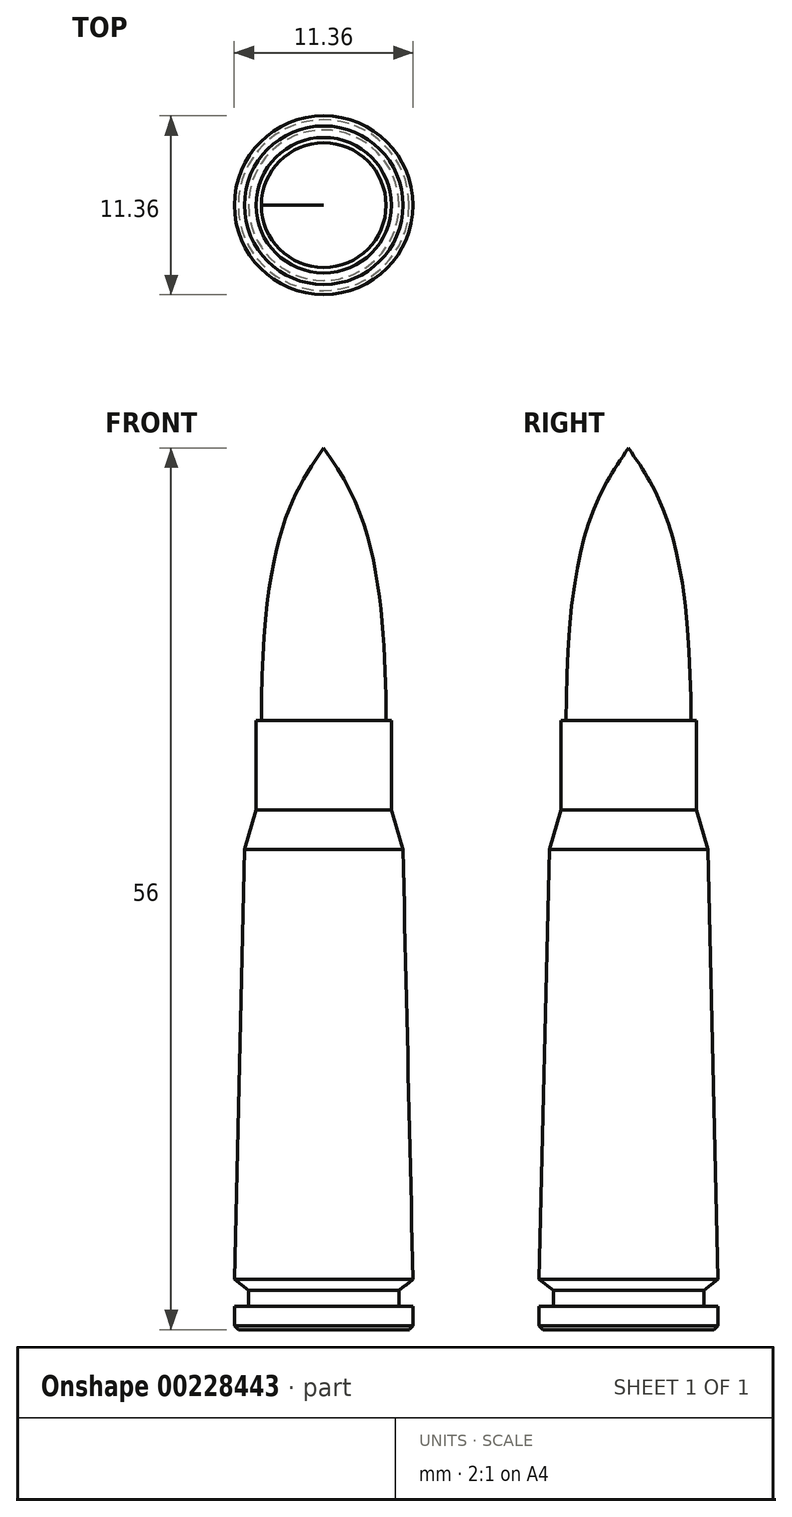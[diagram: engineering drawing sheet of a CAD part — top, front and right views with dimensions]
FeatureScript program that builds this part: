
annotation { "Feature Type Name" : "Feature", "Feature Type Description" : "" }
export const myFeature = defineFeature(function(context is Context, id is Id, definition is map)
    precondition{}
    {
        {
            var Q0;
            Q0=qCreatedBy(makeId("Top.planeOp"),FACE);
            cPlane(context, id + "F0", {"entities" : qUnion([Q0]), "cplaneType" : CPlaneType.OFFSET, "offset" : 38.7 * mm, "oppositeDirection" : true, "width" : 152.4 * mm, "height" : 152.4 * mm});
        }
        {
            var Q0;
            Q0=qCreatedBy(id+"F0.planeOp",FACE);
            cPlane(context, id + "F1", {"entities" : qUnion([Q0]), "cplaneType" : CPlaneType.OFFSET, "offset" : 56 * mm, "width" : 150 * mm, "height" : 150 * mm});
        }
        {
            var Q0;
            Q0=qCreatedBy(id+"F1.planeOp",FACE);
            var sketch = newSketch(context, id + "F2", { "sketchPlane" : qUnion([Q0])});
            skPoint(sketch, "E0", {"position": v(0, 0) * mm});
            skSolve(sketch);
        }
        {
            var Q0;
            Q0=qCreatedBy(makeId("Top.planeOp"),FACE);
            var sketch = newSketch(context, id + "F3", { "sketchPlane" : qUnion([Q0])});
            skCircle(sketch, "E1", {"center": v(0, 0) * mm, "radius": 3.96 * mm});
            skSolve(sketch);
        }
        {
            var Q0;
            Q0=makeQuery(id+"F3.imprint","IMPRINT",FACE,{"disambiguationData":[TD([[makeQuery(id+"F3.imprint","IMPRINT",EDGE,{"derivedFrom":sQuery(id+"F3.wireOp",EDGE,"E1")}),1.0]])]});
            var Q1;
            Q1=sQuery(id+"F2.wireOp",VERTEX,"E0");
            loft(context, id + "F4", {"startCondition" : LoftEndDerivativeType.NORMAL_TO_PROFILE, "startMagnitude" : 2, "sheetProfilesArray" : [{ "sheetProfileEntities" : qUnion([Q0]) }, { "sheetProfileEntities" : qUnion([Q1]) }]});
        }
        {
            var Q0;
            Q0=qCreatedBy(makeId("Top.planeOp"),FACE);
            var sketch = newSketch(context, id + "F5", { "sketchPlane" : qUnion([Q0])});
            skCircle(sketch, "E2", {"center": v(0, 0) * mm, "radius": 4.3 * mm});
            skSolve(sketch);
        }
        {
            var Q0;
            Q0=qCreatedBy(id+"F0.planeOp",FACE);
            cPlane(context, id + "F6", {"entities" : qUnion([Q0]), "cplaneType" : CPlaneType.OFFSET, "offset" : 33 * mm, "width" : 150 * mm, "height" : 150 * mm});
        }
        {
            var Q0;
            Q0=qCreatedBy(id+"F6.planeOp",FACE);
            var sketch = newSketch(context, id + "F7", { "sketchPlane" : qUnion([Q0])});
            skCircle(sketch, "E3", {"center": v(0, 0) * mm, "radius": 4.3 * mm});
            skSolve(sketch);
        }
        {
            var Q1;
            Q1=makeQuery(id+"F7.imprint","IMPRINT",FACE,{"disambiguationData":[TD([[makeQuery(id+"F7.imprint","IMPRINT",EDGE,{"derivedFrom":sQuery(id+"F7.wireOp",EDGE,"E3")}),1.0]])]});
            var Q2;
            Q2=makeQuery(id+"F5.imprint","IMPRINT",FACE,{"disambiguationData":[TD([[makeQuery(id+"F5.imprint","IMPRINT",EDGE,{"derivedFrom":sQuery(id+"F5.wireOp",EDGE,"E2")}),1.0]])]});
            loft(context, id + "F8", {"operationType" : NewBodyOperationType.ADD, "sheetProfilesArray" : [{ "sheetProfileEntities" : qUnion([Q1]) }, { "sheetProfileEntities" : qUnion([Q2]) }]});
        }
        {
            var Q0;
            Q0=qCreatedBy(id+"F0.planeOp",FACE);
            cPlane(context, id + "F9", {"entities" : qUnion([Q0]), "cplaneType" : CPlaneType.OFFSET, "offset" : 30.5 * mm, "width" : 150 * mm, "height" : 150 * mm});
        }
        {
            var Q0;
            Q0=qCreatedBy(id+"F9.planeOp",FACE);
            var sketch = newSketch(context, id + "F10", { "sketchPlane" : qUnion([Q0])});
            skCircle(sketch, "E4", {"center": v(0, 0) * mm, "radius": 5.04 * mm});
            skSolve(sketch);
        }
        {
            var Q1;
            Q1=makeQuery(id+"F10.imprint","IMPRINT",FACE,{"disambiguationData":[TD([[makeQuery(id+"F10.imprint","IMPRINT",EDGE,{"derivedFrom":sQuery(id+"F10.wireOp",EDGE,"E4")}),1.0]])]});
            var Q2;
            Q2=makeQuery(id+"F8.opLoft","CAP_FACE",FACE,{"disambiguationData":[OSD([makeQuery(id+"F7.imprint","IMPRINT",FACE,{"disambiguationData":[TD([[makeQuery(id+"F7.imprint","IMPRINT",EDGE,{"derivedFrom":sQuery(id+"F7.wireOp",EDGE,"E3")}),1.0]])]})])],"isStart":true});
            loft(context, id + "F11", {"operationType" : NewBodyOperationType.ADD, "sheetProfilesArray" : [{ "sheetProfileEntities" : qUnion([Q1]) }, { "sheetProfileEntities" : qUnion([Q2]) }]});
        }
        {
            var Q0;
            Q0=qCreatedBy(id+"F0.planeOp",FACE);
            cPlane(context, id + "F12", {"entities" : qUnion([Q0]), "cplaneType" : CPlaneType.OFFSET, "offset" : 3.2 * mm, "width" : 150 * mm, "height" : 150 * mm});
        }
        {
            var Q0;
            Q0=qCreatedBy(id+"F12.planeOp",FACE);
            var sketch = newSketch(context, id + "F13", { "sketchPlane" : qUnion([Q0])});
            skCircle(sketch, "E5", {"center": v(0, 0) * mm, "radius": 5.68 * mm});
            skSolve(sketch);
        }
        {
            var Q1;
            Q1=makeQuery(id+"F13.imprint","IMPRINT",FACE,{"disambiguationData":[TD([[makeQuery(id+"F13.imprint","IMPRINT",EDGE,{"derivedFrom":sQuery(id+"F13.wireOp",EDGE,"E5")}),1.0]])]});
            var Q2;
            Q2=makeQuery(id+"F11.opLoft","CAP_FACE",FACE,{"disambiguationData":[OSD([makeQuery(id+"F10.imprint","IMPRINT",FACE,{"disambiguationData":[TD([[makeQuery(id+"F10.imprint","IMPRINT",EDGE,{"derivedFrom":sQuery(id+"F10.wireOp",EDGE,"E4")}),1.0]])]})])],"isStart":true});
            loft(context, id + "F14", {"operationType" : NewBodyOperationType.ADD, "sheetProfilesArray" : [{ "sheetProfileEntities" : qUnion([Q1]) }, { "sheetProfileEntities" : qUnion([Q2]) }]});
        }
        {
            var Q0;
            Q0=qCreatedBy(id+"F0.planeOp",FACE);
            cPlane(context, id + "F15", {"entities" : qUnion([Q0]), "cplaneType" : CPlaneType.OFFSET, "offset" : 2.5 * mm, "width" : 150 * mm, "height" : 150 * mm});
        }
        {
            var Q0;
            Q0=qCreatedBy(id+"F15.planeOp",FACE);
            var sketch = newSketch(context, id + "F16", { "sketchPlane" : qUnion([Q0])});
            skCircle(sketch, "E6", {"center": v(0, 0) * mm, "radius": 4.78 * mm});
            skSolve(sketch);
        }
        {
            var Q1;
            Q1 = qSketchRegion(id + "F16", true);
            var Q2;
            Q2=makeQuery(id+"F14.opLoft","CAP_FACE",FACE,{"disambiguationData":[OSD([makeQuery(id+"F13.imprint","IMPRINT",FACE,{"disambiguationData":[TD([[makeQuery(id+"F13.imprint","IMPRINT",EDGE,{"derivedFrom":sQuery(id+"F13.wireOp",EDGE,"E5")}),1.0]])]})])],"isStart":true});
            loft(context, id + "F17", {"operationType" : NewBodyOperationType.ADD, "sheetProfilesArray" : [{ "sheetProfileEntities" : qUnion([Q1]) }, { "sheetProfileEntities" : qUnion([Q2]) }]});
        }
        {
            var Q0;
            Q0=makeQuery(id+"F17.opLoft","CAP_FACE",FACE,{"disambiguationData":[OSD([makeQuery(id+"F16.imprint","IMPRINT",FACE,{"disambiguationData":[TD([[makeQuery(id+"F16.imprint","IMPRINT",EDGE,{"derivedFrom":sQuery(id+"F16.wireOp",EDGE,"E6")}),1.0]])]})])],"isStart":true});
            extrude(context, id + "F18", {"entities" : qUnion([Q0]), "operationType" : NewBodyOperationType.ADD, "depth" : 1 * mm});
        }
        {
            var Q0;
            Q0=qCreatedBy(id+"F0.planeOp",FACE);
            cPlane(context, id + "F19", {"entities" : qUnion([Q0]), "cplaneType" : CPlaneType.OFFSET, "offset" : 1.5 * mm, "width" : 150 * mm, "height" : 150 * mm});
        }
        {
            var Q0;
            Q0=qCreatedBy(id+"F19.planeOp",FACE);
            var sketch = newSketch(context, id + "F20", { "sketchPlane" : qUnion([Q0])});
            skCircle(sketch, "E7", {"center": v(0, 0) * mm, "radius": 5.68 * mm});
            skSolve(sketch);
        }
        {
            var Q0;
            Q0=makeQuery(id+"F20.imprint","IMPRINT",FACE,{"disambiguationData":[TD([[makeQuery(id+"F20.imprint","IMPRINT",EDGE,{"derivedFrom":sQuery(id+"F20.wireOp",EDGE,"E7")}),1.0]])]});
            extrude(context, id + "F21", {"entities" : qUnion([Q0]), "operationType" : NewBodyOperationType.ADD, "oppositeDirection" : true, "depth" : 1.25 * mm});
        }
        {
            var Q0;
            Q0=qCreatedBy(id+"F0.planeOp",FACE);
            var sketch = newSketch(context, id + "F22", { "sketchPlane" : qUnion([Q0])});
            skCircle(sketch, "E8", {"center": v(0, 0) * mm, "radius": 5.42 * mm});
            skSolve(sketch);
        }
        {
            var Q1;
            Q1=makeQuery(id+"F22.imprint","IMPRINT",FACE,{"disambiguationData":[TD([[makeQuery(id+"F22.imprint","IMPRINT",EDGE,{"derivedFrom":sQuery(id+"F22.wireOp",EDGE,"E8")}),1.0]])]});
            var Q2;
            Q2=makeQuery(id+"F21.opExtrude","CAP_FACE",FACE,{"disambiguationData":[OSD([sQuery(id+"F20.wireOp",EDGE,"E7")])],"isStart":false});
            loft(context, id + "F23", {"operationType" : NewBodyOperationType.ADD, "sheetProfilesArray" : [{ "sheetProfileEntities" : qUnion([Q1]) }, { "sheetProfileEntities" : qUnion([Q2]) }]});
        }
    });
